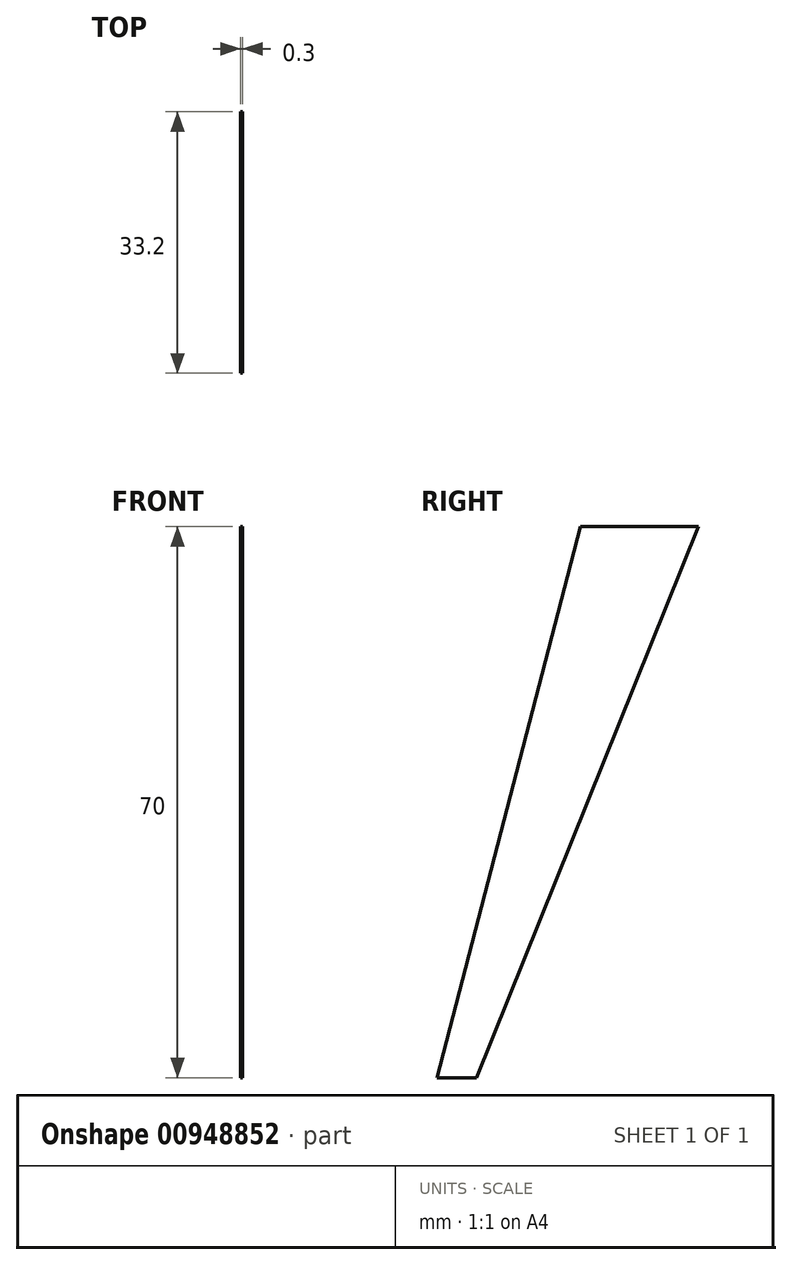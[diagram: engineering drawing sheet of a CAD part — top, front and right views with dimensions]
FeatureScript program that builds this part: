
annotation { "Feature Type Name" : "Feature", "Feature Type Description" : "" }
export const myFeature = defineFeature(function(context is Context, id is Id, definition is map)
    precondition{}
    {
        {
            var Q0;
            Q0=qCreatedBy(makeId("Right.planeOp"),FACE);
            var sketch = newSketch(context, id + "F0", { "sketchPlane" : qUnion([Q0])});
            skLineSegment(sketch, "E0.bottom", {"start": v(1.6, 35) * mm, "end": v(16.6, 35) * mm});
            skLineSegment(sketch, "E0.top", {"start": v(-16.6, -35) * mm, "end": v(-11.6, -35) * mm});
            skPoint(sketch, "E0.middle", {"position": v(0, 0) * mm});
            skLineSegment(sketch, "E1", {"start": v(1.6, 35) * mm, "end": v(-16.6, -35) * mm});
            skLineSegment(sketch, "E2", {"start": v(16.6, 35) * mm, "end": v(-11.6, -35) * mm});
            skPoint(sketch, "E3.orphan", {"position": v(-16.6, 35) * mm});
            skPoint(sketch, "E4.orphan", {"position": v(16.6, -35) * mm});
            skSolve(sketch);
        }
        {
            var Q0;
            Q0 = qSketchRegion(id + "F0", true);
            extrude(context, id + "F1", {"entities" : qUnion([Q0]), "depth" : 0.3 * mm, "offsetDistance" : 25 * mm});
        }
    });
